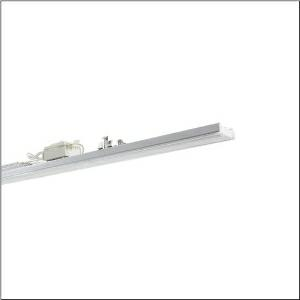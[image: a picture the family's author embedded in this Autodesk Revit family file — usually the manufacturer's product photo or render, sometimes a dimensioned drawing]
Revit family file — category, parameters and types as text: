
# Revit family: licross_r__21_recessed_mo_52tl10cn49xg_3ade
name_source: partatom
category: Lighting Fixtures
units: mm (PartAtom-declared; Revit-internal decimal feet)

## family parameters
Cut with Voids When Loaded = No
Host = Face
Light Source = No
Part Type = Normal
Room Calculation Point = No
Round Connector Dimension = Use Diameter
Shared = No

## types (1)
- --- (1 x LED, 9010 lm, 49.9 W, 4000K)
    Apparent Load = 50 VA
    CIE Flux Codes = 50 81 96 100 100
    Color Rendering = 80
    Color Temperature = 4000K
    Default Elevation = 1800 mm
    Description = Licross® 21 Recessed MO, luminaire insert, of sheet steel, galvanised, coil coated, white, length: 1.500mm, width: 66mm, height: 67mm, LED rated luminous flux: 9.010lm, light colour: 840, control gear: ON/OFF Multilumen, CLOi, control gear: ECG Multilumen, with plug, 3-pole, with phase selection, mains connection: 220..240V, AC, 50/60Hz, start of lifetime: 49W, end of service life: 61W, halogen-free wiring, primary optical cover: cover, of PMMA, light emission: direct distribution, primary light characteristic: symmetric, protection rating (complete): IP40, insulation class (complete): insulation class I (protective earthing), certification: CE, ENEC, VDE, UKCA, protection symbol: D if used in an environment without relevant dust loads with corresponding accessories, impact resistance: IK06, permissible ambient temperature for indoor applications: -35..+40°C, corresponds to IFS (International Featured Standards) requirements for safety and quality in the food industry, reducing of maximum allowable ambient temperature of 5°C with ceiling mounting, LABS conformity tested according to VDMA 24364:2018-05, packaging unit: 1 piece
    Height = 58 mm
    Lamp = 1 x LED
    Lamp Light Flux = 9010 lm
    Lamp Power = 49.9 W
    Lamp count = 1
    Length = 1500 mm
    Luminous efficacy = 181 lm/W
    Manufacturer = Siteco
    ModVariant = No
    Model = 52TL10CN49XG
    Mounting Place = Ceiling
    Mounting Type = Pendant
    Number of Poles = 1
    OnlyDefault = Yes
    Power Factor = 1
    Product Name = Licross® 21 Recessed MO
    Product group = luminaire insert
    ProductGroupID = 902
    Protection Class = Protection class I
    Protection Degree = IP 40
    RLX_Detail_Level = 1
    RLX_Emergency_Light_Flux = 0 lm
    RLX_Emergency_Type = 0
    RLX_Emergency_Type_DB = No
    RlxData = <blob elided: 22137 chars, md5=394a9ff1>
    Socket = socket
    Standby Power = 0 W
    System Light Flux = 9010 lm
    System Power = 50 W
    Type Comments = factory setting: luminous flux: 100 % | (A | C | E) | 116 mA
    Type Image = l_1296930.jpg
    URL = http://relux.com
    VarID = @adj_110750
    Voltage = 0 V
    Weight = 0.00 kg
    Width = 66 mm

## geometry (parser evidence)
native form markers: Blend x4, Sweep x11
no freeform markers — native parametric forms only
